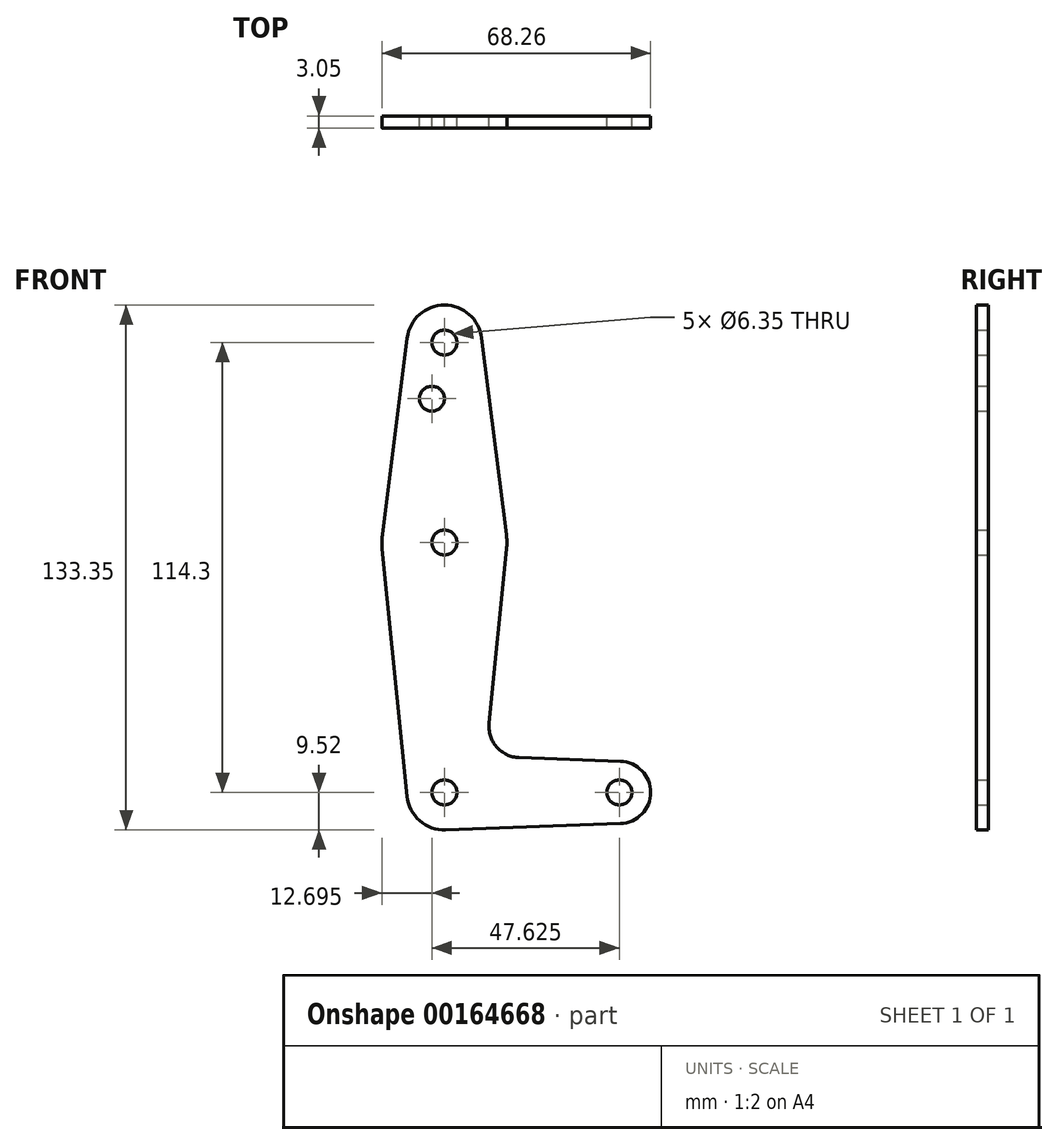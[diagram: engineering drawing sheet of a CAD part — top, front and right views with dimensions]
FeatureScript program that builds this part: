
annotation { "Feature Type Name" : "Feature", "Feature Type Description" : "" }
export const myFeature = defineFeature(function(context is Context, id is Id, definition is map)
    precondition{}
    {
        {
            var Q0;
            Q0=qCreatedBy(makeId("Front.planeOp"),FACE);
            var sketch = newSketch(context, id + "F0", { "sketchPlane" : qUnion([Q0])});
            skLineSegment(sketch, "E0", {"start": v(0, 0) * mm, "end": v(0, 114.3) * mm, "construction": true});
            skLineSegment(sketch, "E1", {"start": v(0, 0) * mm, "end": v(44.45, 0) * mm, "construction": true});
            skCircle(sketch, "E2", {"center": v(0, 0) * mm, "radius": 9.53 * mm});
            skCircle(sketch, "E3", {"center": v(0, 63.5) * mm, "radius": 15.88 * mm});
            skCircle(sketch, "E4", {"center": v(0, 114.3) * mm, "radius": 9.53 * mm});
            skCircle(sketch, "E5", {"center": v(44.45, 0) * mm, "radius": 7.94 * mm});
            skLineSegment(sketch, "E6", {"start": v(-9.45, 115.5) * mm, "end": v(-15.75, 65.48) * mm});
            skLineSegment(sketch, "E7", {"start": v(9.45, 115.5) * mm, "end": v(15.75, 65.48) * mm});
            skLineSegment(sketch, "E8", {"start": v(15.8, 61.91) * mm, "end": v(11.34, 17.6) * mm});
            skLineSegment(sketch, "E9", {"start": v(-15.8, 61.91) * mm, "end": v(-9.48, -0.95) * mm});
            skLineSegment(sketch, "E10", {"start": v(0.34, -9.52) * mm, "end": v(44.73, -7.93) * mm});
            skLineSegment(sketch, "E11", {"start": v(18.97, 8.85) * mm, "end": v(44.73, 7.93) * mm});
            skCircle(sketch, "E12", {"center": v(0, 114.3) * mm, "radius": 3.18 * mm});
            skCircle(sketch, "E13", {"center": v(-3.18, 100.03) * mm, "radius": 3.18 * mm});
            skCircle(sketch, "E14", {"center": v(0, 63.5) * mm, "radius": 3.18 * mm});
            skCircle(sketch, "E15", {"center": v(0, 0) * mm, "radius": 3.18 * mm});
            skCircle(sketch, "E16", {"center": v(44.45, 0) * mm, "radius": 3.18 * mm});
            skArc(sketch, "E17.filletArc", {"start": v(11.34, 17.6) * mm, "mid": v(13.26, 11.57) * mm, "end": v(18.97, 8.85) * mm});
            skSolve(sketch);
        }
        {
            var Q0;
            Q0 = qSketchRegion(id + "F0", true);
            extrude(context, id + "F1", {"entities" : qUnion([Q0]), "depth" : 3.05 * mm});
        }
    });
